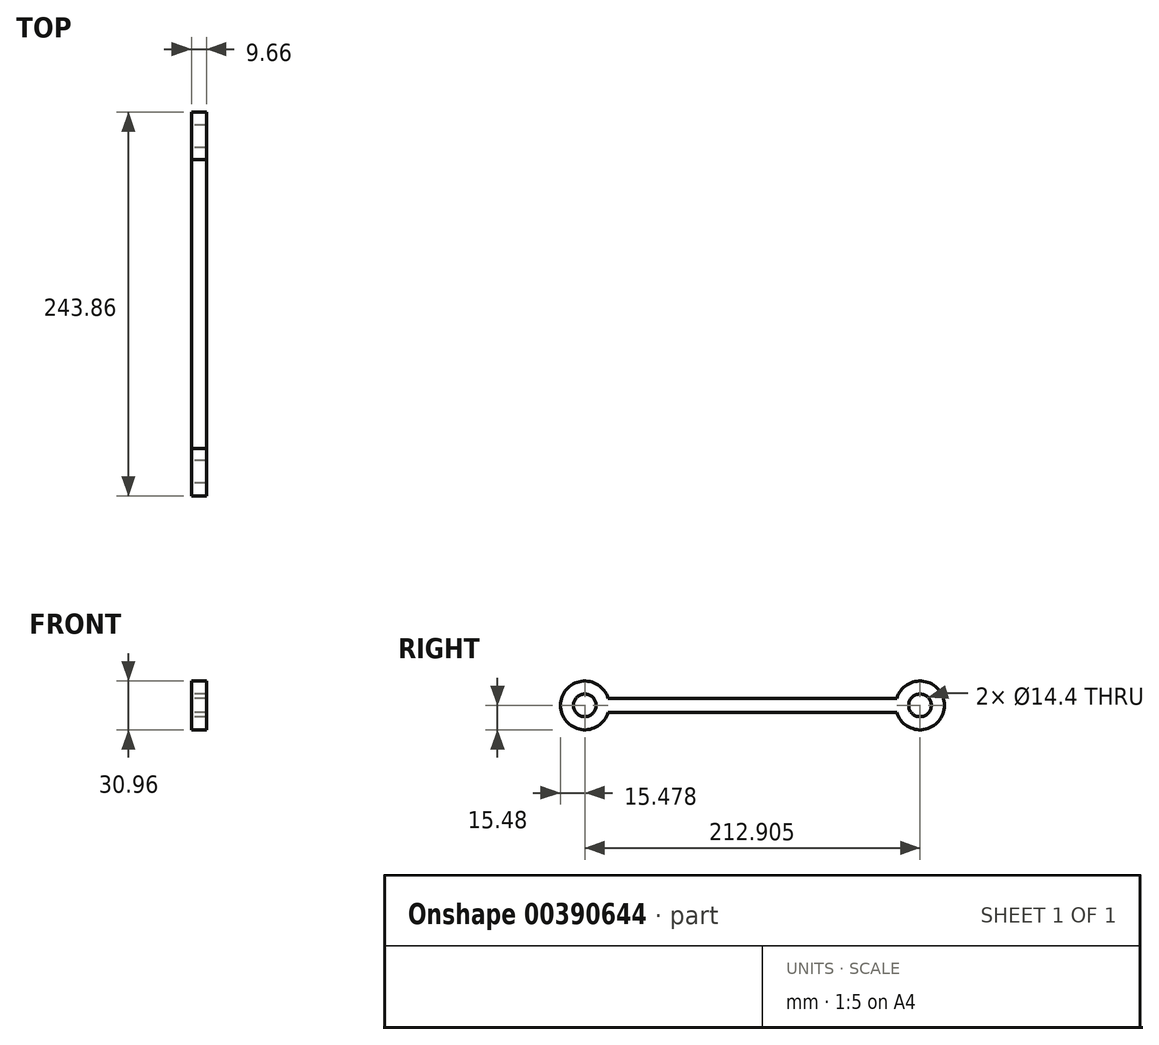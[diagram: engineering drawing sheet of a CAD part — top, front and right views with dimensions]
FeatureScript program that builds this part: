
annotation { "Feature Type Name" : "Feature", "Feature Type Description" : "" }
export const myFeature = defineFeature(function(context is Context, id is Id, definition is map)
    precondition{}
    {
        {
            var Q0;
            Q0=qCreatedBy(makeId("Right.planeOp"),FACE);
            var sketch = newSketch(context, id + "F0", { "sketchPlane" : qUnion([Q0])});
            skLineSegment(sketch, "E0.bottom", {"start": v(0, 4.54) * mm, "end": v(-91.65, 4.54) * mm});
            skLineSegment(sketch, "E0.top", {"start": v(0, -4.54) * mm, "end": v(-91.65, -4.54) * mm});
            skLineSegment(sketch, "E0.left", {"start": v(0, 4.54) * mm, "end": v(0, -4.54) * mm});
            skPoint(sketch, "E0.middle", {"position": v(-53.23, 0) * mm});
            skCircle(sketch, "E1", {"center": v(-106.45, 0) * mm, "radius": 7.2 * mm});
            skArc(sketch, "E2", {"start": v(-91.65, 4.54) * mm, "mid": v(-121.93, 0) * mm, "end": v(-91.65, -4.54) * mm});
            skSolve(sketch);
        }
        {
            var Q0;
            Q0 = qSketchRegion(id + "F0", true);
            extrude(context, id + "F1", {"entities" : qUnion([Q0]), "depth" : 4.83 * mm});
        }
        {
            var Q0;
            Q0=makeQuery(id+"F1.opExtrude","SWEPT_BODY",BODY,{"disambiguationData":[OSD([sQuery(id+"F0.wireOp",EDGE,"E0.bottom"),sQuery(id+"F0.wireOp",EDGE,"E0.top"),sQuery(id+"F0.wireOp",EDGE,"E0.left"),sQuery(id+"F0.wireOp",EDGE,"E1"),sQuery(id+"F0.wireOp",EDGE,"E2")])]});
            var Q1;
            Q1=qCreatedBy(makeId("Right.planeOp"),FACE);
            mirror(context, id + "F2", {"operationType" : NewBodyOperationType.ADD, "entities" : qUnion([Q0]), "mirrorPlane" : qUnion([Q1])});
        }
        {
            var Q0;
            Q0=makeQuery(id+"F1.opExtrude","SWEPT_BODY",BODY,{"disambiguationData":[OSD([sQuery(id+"F0.wireOp",EDGE,"E0.bottom"),sQuery(id+"F0.wireOp",EDGE,"E0.top"),sQuery(id+"F0.wireOp",EDGE,"E0.left"),sQuery(id+"F0.wireOp",EDGE,"E1"),sQuery(id+"F0.wireOp",EDGE,"E2")])]});
            var Q1;
            Q1=qCreatedBy(makeId("Front.planeOp"),FACE);
            mirror(context, id + "F3", {"operationType" : NewBodyOperationType.ADD, "entities" : qUnion([Q0]), "mirrorPlane" : qUnion([Q1])});
        }
    });
